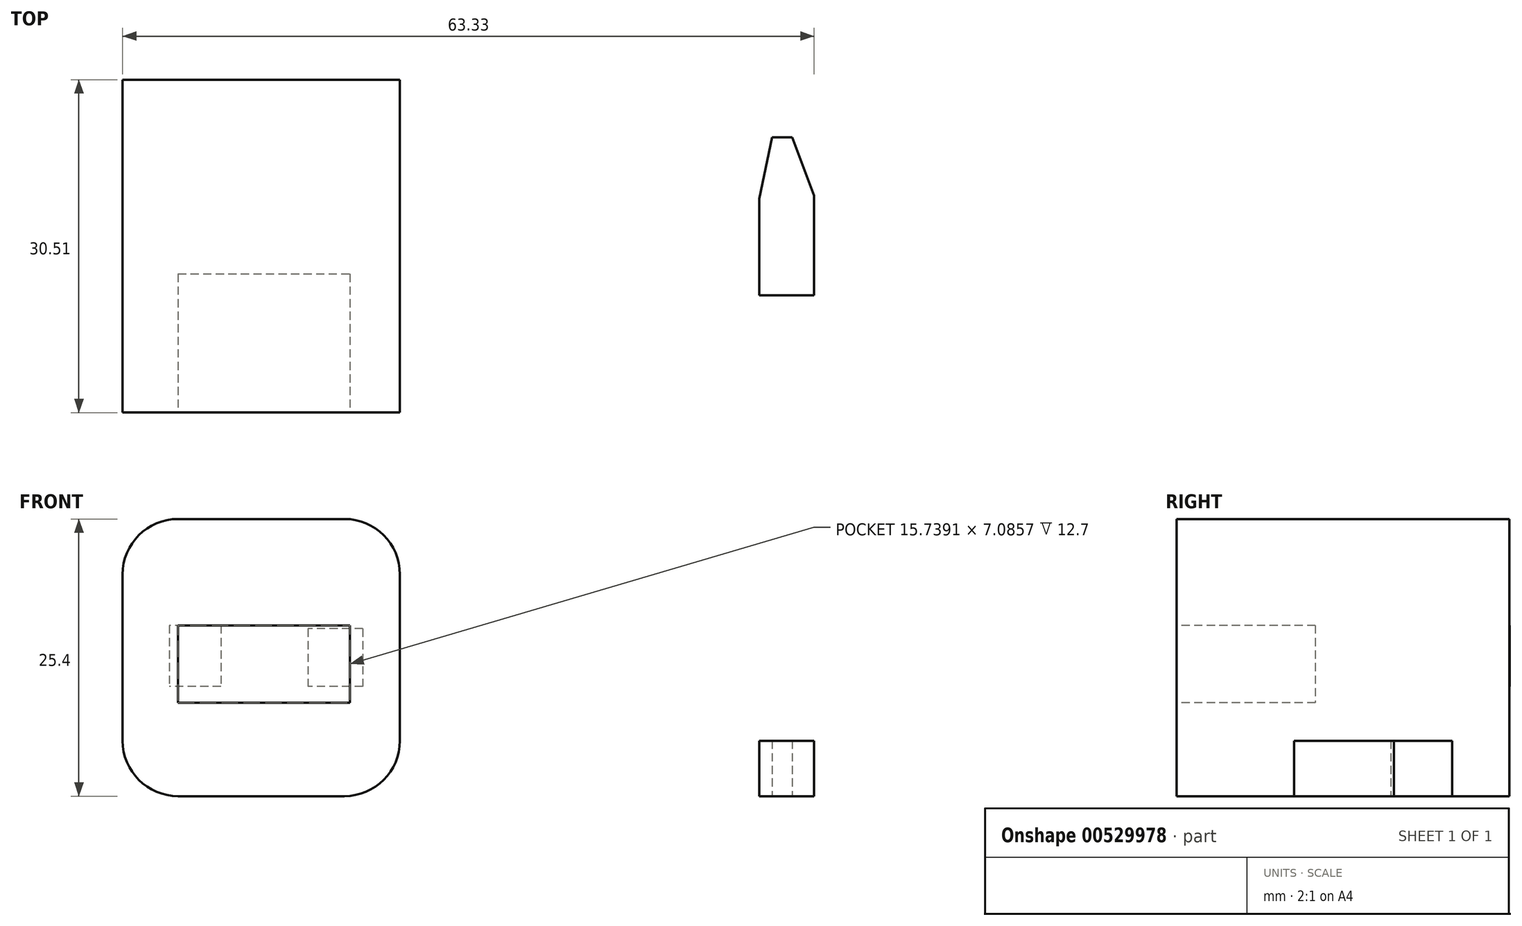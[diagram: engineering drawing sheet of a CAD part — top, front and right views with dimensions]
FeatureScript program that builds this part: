
annotation { "Feature Type Name" : "Feature", "Feature Type Description" : "" }
export const myFeature = defineFeature(function(context is Context, id is Id, definition is map)
    precondition{}
    {
        {
            var Q0;
            Q0=qCreatedBy(makeId("Top.planeOp"),FACE);
            var sketch = newSketch(context, id + "F0", { "sketchPlane" : qUnion([Q0])});
            skLineSegment(sketch, "E0.bottom", {"start": v(-42.96, 36.85) * mm, "end": v(-17.56, 36.85) * mm});
            skLineSegment(sketch, "E0.top", {"start": v(-42.96, 6.37) * mm, "end": v(-17.56, 6.37) * mm});
            skLineSegment(sketch, "E0.left", {"start": v(-42.96, 36.85) * mm, "end": v(-42.96, 6.37) * mm});
            skLineSegment(sketch, "E0.right", {"start": v(-17.56, 36.85) * mm, "end": v(-17.56, 6.37) * mm});
            skSolve(sketch);
        }
        {
            var Q0;
            Q0 = qSketchRegion(id + "F0", true);
            extrude(context, id + "F1", {"entities" : qUnion([Q0]), "depth" : 25.4 * mm, "offsetDistance" : 25.4 * mm});
        }
        {
            var Q0;
            Q0=makeQuery(id+"F1.opExtrude","CAP_EDGE",EDGE,{"disambiguationData":[OSD([sQuery(id+"F0.wireOp",EDGE,"E0.left")])],"isStart":false});
            fillet(context, id + "F2", {"entities" : qUnion([Q0]), "radius" : 5.08 * mm, "tangentPropagation" : true, "allowEdgeOverflow" : false});
        }
        {
            var Q0;
            Q0=makeQuery(id+"F1.opExtrude","CAP_EDGE",EDGE,{"disambiguationData":[OSD([sQuery(id+"F0.wireOp",EDGE,"E0.left")])],"isStart":true});
            var Q1;
            Q1=makeQuery(id+"F1.opExtrude","CAP_EDGE",EDGE,{"disambiguationData":[OSD([sQuery(id+"F0.wireOp",EDGE,"E0.right")])],"isStart":true});
            var Q2;
            Q2=makeQuery(id+"F1.opExtrude","CAP_EDGE",EDGE,{"disambiguationData":[OSD([sQuery(id+"F0.wireOp",EDGE,"E0.right")])],"isStart":false});
            fillet(context, id + "F3", {"entities" : qUnion([Q0, Q1, Q2]), "radius" : 5.08 * mm, "tangentPropagation" : true, "allowEdgeOverflow" : false});
        }
        {
            var Q0;
            Q0=qCreatedBy(makeId("Top.planeOp"),FACE);
            var sketch = newSketch(context, id + "F4", { "sketchPlane" : qUnion([Q0])});
            skLineSegment(sketch, "E1", {"start": v(15.35, 17.12) * mm, "end": v(15.35, 25.98) * mm});
            skLineSegment(sketch, "E2", {"start": v(20.37, 17.12) * mm, "end": v(20.37, 26.28) * mm});
            skPoint(sketch, "E3", {"position": v(16.53, 31.6) * mm});
            skPoint(sketch, "E4", {"position": v(18.36, 31.6) * mm});
            skLineSegment(sketch, "E5", {"start": v(15.35, 25.98) * mm, "end": v(16.53, 31.6) * mm});
            skLineSegment(sketch, "E6", {"start": v(18.36, 31.6) * mm, "end": v(20.37, 26.28) * mm});
            skLineSegment(sketch, "E7", {"start": v(15.35, 17.12) * mm, "end": v(20.37, 17.12) * mm});
            skLineSegment(sketch, "E8", {"start": v(18.36, 31.6) * mm, "end": v(16.53, 31.6) * mm});
            skSolve(sketch);
        }
        {
            var Q0;
            Q0 = qSketchRegion(id + "F4", true);
            extrude(context, id + "F5", {"entities" : qUnion([Q0]), "depth" : 5.08 * mm, "offsetDistance" : 25.4 * mm});
        }
        {
            var Q0;
            Q0=makeQuery(id+"F1.opExtrude","SWEPT_FACE",FACE,{"disambiguationData":[OSD([sQuery(id+"F0.wireOp",EDGE,"E0.top")])]});
            var sketch = newSketch(context, id + "F6", { "sketchPlane" : qUnion([Q0])});
            skLineSegment(sketch, "E9.bottom", {"start": v(-37.88, 15.65) * mm, "end": v(-22.14, 15.65) * mm});
            skLineSegment(sketch, "E9.top", {"start": v(-37.88, 8.56) * mm, "end": v(-22.14, 8.56) * mm});
            skLineSegment(sketch, "E9.left", {"start": v(-37.88, 15.65) * mm, "end": v(-37.88, 8.56) * mm});
            skLineSegment(sketch, "E9.right", {"start": v(-22.14, 15.65) * mm, "end": v(-22.14, 8.56) * mm});
            skSolve(sketch);
        }
        {
            var Q0;
            Q0=makeQuery(id+"F6.imprint","IMPRINT",FACE,{"disambiguationData":[TD([[makeQuery(id+"F6.imprint","IMPRINT",EDGE,{"derivedFrom":sQuery(id+"F6.wireOp",EDGE,"E9.bottom")}),-1.0]])]});
            extrude(context, id + "F7", {"entities" : qUnion([Q0]), "operationType" : NewBodyOperationType.REMOVE, "oppositeDirection" : true, "depth" : 12.7 * mm, "offsetDistance" : 25.4 * mm});
        }
        {
            var Q0;
            Q0=makeQuery(id+"F1.opExtrude","SWEPT_FACE",FACE,{"disambiguationData":[OSD([sQuery(id+"F0.wireOp",EDGE,"E0.bottom")])]});
            var sketch = newSketch(context, id + "F8", { "sketchPlane" : qUnion([Q0])});
            skLineSegment(sketch, "E10.bottom", {"start": v(33.95, 15.65) * mm, "end": v(38.68, 15.65) * mm});
            skLineSegment(sketch, "E10.top", {"start": v(33.95, 10.04) * mm, "end": v(38.68, 10.04) * mm});
            skLineSegment(sketch, "E10.left", {"start": v(33.95, 15.65) * mm, "end": v(33.95, 10.04) * mm});
            skLineSegment(sketch, "E10.right", {"start": v(38.68, 15.65) * mm, "end": v(38.68, 10.04) * mm});
            skLineSegment(sketch, "E11.bottom", {"start": v(20.96, 15.35) * mm, "end": v(25.98, 15.35) * mm});
            skLineSegment(sketch, "E11.top", {"start": v(20.96, 10.04) * mm, "end": v(25.98, 10.04) * mm});
            skLineSegment(sketch, "E11.left", {"start": v(20.96, 15.35) * mm, "end": v(20.96, 10.04) * mm});
            skLineSegment(sketch, "E11.right", {"start": v(25.98, 15.35) * mm, "end": v(25.98, 10.04) * mm});
            skSolve(sketch);
        }
        {
            var Q0;
            Q0=makeQuery(id+"F8.imprint","IMPRINT",FACE,{"disambiguationData":[TD([[makeQuery(id+"F8.imprint","IMPRINT",EDGE,{"derivedFrom":sQuery(id+"F8.wireOp",EDGE,"E10.bottom")}),-1.0]])]});
            var Q1;
            Q1=makeQuery(id+"F8.imprint","IMPRINT",FACE,{"disambiguationData":[TD([[makeQuery(id+"F8.imprint","IMPRINT",EDGE,{"derivedFrom":sQuery(id+"F8.wireOp",EDGE,"E11.bottom")}),-1.0]])]});
            extrude(context, id + "F9", {"entities" : qUnion([Q0, Q1]), "operationType" : NewBodyOperationType.ADD, "depth" : 0.03 * mm, "offsetDistance" : 25.4 * mm});
        }
    });
